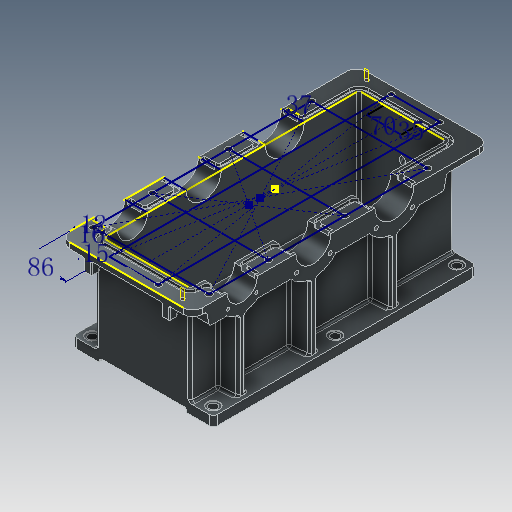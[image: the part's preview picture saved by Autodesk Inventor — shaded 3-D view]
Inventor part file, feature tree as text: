
AUTODESK INVENTOR PART (.ipt)
format: ipt  version: 2025 (Build 290162000, 162)  size: 1,567,232 bytes
history: native  units: mm
features: sketch x25, reference x17, other x15, extrude x15, hole x8, fillet x5, plane x5, revolve x4, projected_geometry x4, mirror x3, thread x2
ambient origin geometry x8: Origin, YZ Plane, XZ Plane, XY Plane, X Axis, Y Axis, Z Axis, Center Point
bodies: Body1 (feature_tree)
feature tree (103):
  other  "箱体底部"
  extrude  "拉伸1"  Depth=540.0mm
  extrude  "拉伸2"  Depth=194.0mm
  extrude  "拉伸3"  Depth=8.0mm
  extrude  "拉伸4"  Depth=42.0mm
  extrude  "拉伸5"  Depth=62.0mm
  extrude  "拉伸6"  Depth=72.0mm
  fillet  "圆角7"  Radius=80.0mm
  hole  "孔1"  [1 undecoded]
  sketch  "草图8"  dims[d25=6.0mm d26=6.0mm]
  hole  "孔2"  [1 undecoded]
  hole  "孔3"  [1 undecoded]
  extrude  "拉伸7"  Depth=36.0mm
  mirror  "镜像1"
  other  "加强筋1"
  mirror  "镜像2"
  mirror  "镜像3"
  hole  "孔4"  [1 undecoded]
  revolve  "旋转1"  [1 undecoded]
  revolve  "旋转2"  [1 undecoded]
  extrude  "拉伸8"  Depth=8.0mm
  thread  "螺纹1"  [1 undecoded]
  plane  "工作平面1"
  extrude  "拉伸9"  Depth=8.0mm
  fillet  "圆角12"  Radius=11.0mm
  extrude  "拉伸10"  Depth=11.0mm
  thread  "螺纹2"  [1 undecoded]
  extrude  "拉伸11"  Depth=11.0mm
  fillet  "圆角13"  Radius=180.0mm
  fillet  "圆角14"  Radius=8.0mm
  hole  "孔6"  [1 undecoded]
  hole  "孔7"  [1 undecoded]
  hole  "孔8"  [1 undecoded]
  hole  "孔9"  [1 undecoded]
  plane  "工作平面2"
  plane  "工作平面3"
  sketch  "草图25"  dims[d70=86.0mm d73=12.0mm]
  extrude  "拉伸12"  Depth=2.0mm
  extrude  "拉伸13"  Depth=2.0mm
  extrude  "拉伸15"  Depth=2.0mm
  plane  "工作平面4"
  revolve  "旋转3"  [1 undecoded]
  plane  "工作平面5"
  revolve  "旋转4"  [1 undecoded]
  fillet  "圆角15"  Radius=17.715092mm
  sketch  "草图30"  dims[d91=146.0mm d92=102.0mm d93=122.0mm d94=130.0mm d95=40.0mm d96=17.715092mm d97=13.700835mm d98=10.0mm d99=130.0mm d100=0.0mm d101=5.0mm d102=16.0mm d103=10.0mm d104=0.872665mm d105=0.0mm d106=1.0mm d107=1.0mm d108=5.0mm d109=13.0mm d110=6.0mm d111=4.0mm d112=2.0mm d113=90.0deg d114=8.0mm d115=20.594885mm d118=15.0mm d120=125.0mm d121=360.0deg d122=15.0mm d123=12.5mm d124=2.0mm d125=6.0mm d126=360.0deg d127=50.0mm d128=0.0mm d129=20.0mm d130=17.0mm d131=6.0mm d132=26.0mm d133=28.0mm d134=50.0mm d135=0.0mm d136=5.0mm d137=16.0mm d138=10.0mm d139=0.0mm d140=20.0mm d141=0.0mm d142=2.5mm d143=10.0mm d144=10.0mm d145=0.0mm d146=2.0mm d147=0.5mm d155=6.647mm d156=28.0mm d157=4.0mm d158=2.0mm d159=90.0deg d160=30.0mm d161=120.0deg d162=6.647mm d163=28.0mm d164=4.0mm d165=2.0mm d166=90.0deg d167=30.0mm d168=120.0deg d169=8.376mm d170=28.0mm d171=4.0mm d172=2.0mm d173=90.0deg d174=30.0mm d175=120.0deg d176=8.376mm d177=28.0mm d178=4.0mm d179=2.0mm d180=90.0deg d181=30.0mm d182=120.0deg d183=80.0mm d184=-80.0mm d185=27.0mm d186=4.5mm d187=8.5mm d188=17.0mm d189=2.0mm d190=16.0mm d191=0.0mm d192=16.0mm d193=0.0mm d196=10.0mm d197=0.0mm d198=90.0deg d199=90.0deg d200=2.0mm d201=70.0mm d202=35.0mm d203=100.0mm d204=0.0mm d148=0.0mm d149=0.0mm d150=0.0mm d205=0.5mm d206=0.872665mm]
  extrude  "拉伸16"  Depth=2.0mm
  sketch  "草图1"  dims[d0=288.0mm d1=540.0mm]
  sketch  "草图2"  dims[d2=20.0mm d3=0.0mm d4=194.0mm]
  sketch  "草图3"  dims[d5=197.0mm d6=0.0mm d8=8.0mm]
  sketch  "草图4"  dims[d10=47.0mm d11=42.0mm]
  sketch  "草图5"  dims[d12=12.0mm d13=0.0mm d15=62.0mm]
  sketch  "草图6"  dims[d16=0.0mm d17=0.0mm d18=72.0mm d20=80.0mm]
  sketch  "草图7"  dims[d23=20.0mm d24=8.0mm]
  reference  "参考1"
  sketch  "草图11"  dims[d27=8.0mm d28=6.0mm d29=0.0mm]
  projected_geometry  "投影回路1"
  sketch  "草图13"  dims[d31=36.0mm d38=36.0mm]
  projected_geometry  "投影回路2"
  projected_geometry  "投影回路3"
  sketch  "草图14"  dims[d39=36.0mm d40=36.0mm]
  sketch  "草图15"  dims[d41=36.0mm d42=36.0mm]
  sketch  "草图16"  dims[d43=5.0mm d44=8.0mm]
  projected_geometry  "投影回路4"
  sketch  "草图17"  dims[d45=8.0mm d46=8.0mm d47=8.0mm]
  sketch  "草图18"  dims[d48=8.0mm d49=8.0mm d50=11.0mm]
  sketch  "草图19"  dims[d51=11.0mm d52=11.0mm d53=11.0mm]
  sketch  "草图21"  dims[d54=11.0mm d55=11.0mm d56=180.0mm d57=8.0mm d58=0.0mm]
  reference  "参考6"
  reference  "参考7"
  sketch  "草图22"  dims[d59=6.0mm]
  reference  "参考8"
  reference  "参考9"
  sketch  "草图23"  dims[d60=17.0mm d61=6.0mm d62=26.0mm d63=1.5mm d64=90.0deg d65=8.0mm d66=20.594885mm d67=20.0mm]
  reference  "参考10"
  reference  "参考11"
  reference  "参考12"
  reference  "参考13"
  sketch  "草图24"  dims[d68=20.0mm d69=15.0mm]
  reference  "参考14"
  reference  "参考15"
  reference  "参考16"
  reference  "参考17"
  sketch  "草图27"  dims[d74=16.0mm d75=37.0mm]
  sketch  "草图28"  dims[d76=13.0mm d77=6.0mm d78=26.0mm d79=1.5mm d80=90.0deg d81=8.0mm d82=20.594885mm]
  reference  "参考19"
  reference  "参考20"
  sketch  "草图29"  dims[d83=12.0mm d84=6.0mm d85=4.0mm d86=2.0mm d87=90.0deg d88=8.0mm d89=20.594885mm d90=166.25mm]
  reference  "参考21"
  reference  "参考22"
  other  "齿轮箱.iam"
  other  "中间轴:1"
  other  "轴承:2"
  other  "滚动轴承 GB/T 276-1994 60000 和 160000 型 6306:1"
  other  "高速轴承闷盖"
  other  "高速轴承透盖"
  other  "中间轴承闷盖1"
  other  "低速轴承透盖"
  other  "中间轴承闷盖2"
  other  "低速轴承闷盖"
  other  "定位销:1"
  other  "定位销:2"
  other  "<userpath>\Desktop\Inventor files\齿轮箱.iam"
note: 14 required parameter values undecoded (feature->parameter linkage not recoverable at this tier; creation-order binding heuristic only, values carry confidence <= 0.55)